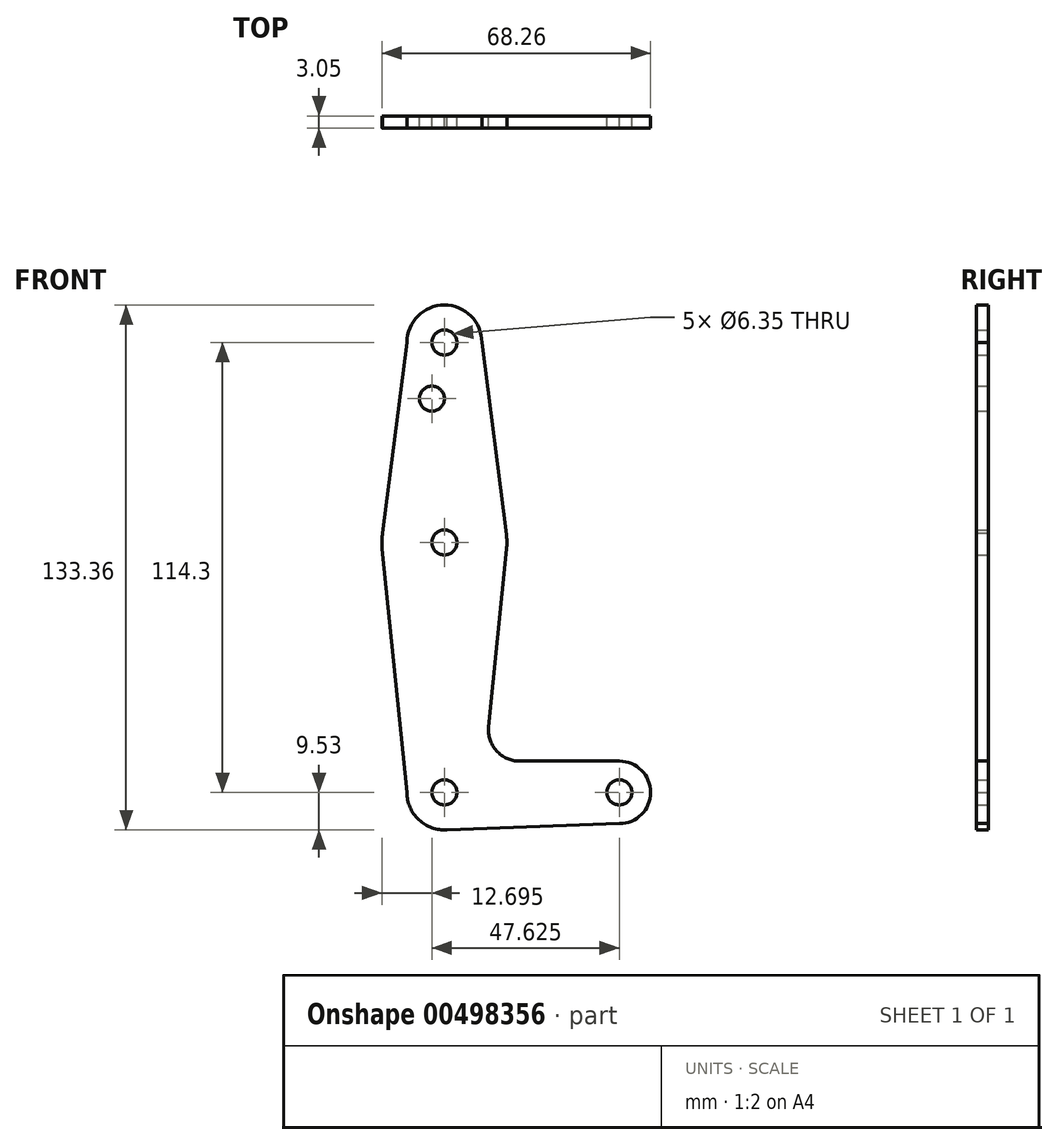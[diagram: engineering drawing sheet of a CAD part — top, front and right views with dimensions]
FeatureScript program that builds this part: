
annotation { "Feature Type Name" : "Feature", "Feature Type Description" : "" }
export const myFeature = defineFeature(function(context is Context, id is Id, definition is map)
    precondition{}
    {
        {
            var Q0;
            Q0=qCreatedBy(makeId("Front.planeOp"),FACE);
            var sketch = newSketch(context, id + "F0", { "sketchPlane" : qUnion([Q0])});
            skLineSegment(sketch, "E0", {"start": v(0, 0) * mm, "end": v(0, 114.3) * mm, "construction": true});
            skLineSegment(sketch, "E1", {"start": v(0, 0) * mm, "end": v(44.45, 0) * mm, "construction": true});
            skCircle(sketch, "E2", {"center": v(0, 114.3) * mm, "radius": 9.53 * mm});
            skCircle(sketch, "E3", {"center": v(0, 63.5) * mm, "radius": 15.88 * mm});
            skCircle(sketch, "E4", {"center": v(0, 0) * mm, "radius": 9.53 * mm});
            skCircle(sketch, "E5", {"center": v(44.45, 0) * mm, "radius": 7.94 * mm});
            skLineSegment(sketch, "E6", {"start": v(-9.53, 0) * mm, "end": v(-15.8, 61.9) * mm});
            skLineSegment(sketch, "E7", {"start": v(-9.53, 114.3) * mm, "end": v(-15.8, 65.1) * mm});
            skLineSegment(sketch, "E8", {"start": v(9.52, 114.3) * mm, "end": v(15.75, 65.5) * mm});
            skLineSegment(sketch, "E9", {"start": v(0, -9.52) * mm, "end": v(44.45, -7.94) * mm});
            skCircle(sketch, "E10", {"center": v(0, 114.3) * mm, "radius": 3.18 * mm});
            skCircle(sketch, "E11", {"center": v(-3.18, 100.03) * mm, "radius": 3.18 * mm});
            skCircle(sketch, "E12", {"center": v(0, 63.5) * mm, "radius": 3.18 * mm});
            skCircle(sketch, "E13", {"center": v(0, 0) * mm, "radius": 3.18 * mm});
            skCircle(sketch, "E14", {"center": v(44.45, 0) * mm, "radius": 3.18 * mm});
            skLineSegment(sketch, "E15", {"start": v(15.8, 61.9) * mm, "end": v(11.22, 16.69) * mm});
            skLineSegment(sketch, "E16", {"start": v(44.45, 7.94) * mm, "end": v(19.12, 7.94) * mm});
            skArc(sketch, "E17.filletArc", {"start": v(11.22, 16.69) * mm, "mid": v(13.23, 10.56) * mm, "end": v(19.12, 7.94) * mm});
            skSolve(sketch);
        }
        {
            var Q0;
            Q0 = qSketchRegion(id + "F0", true);
            extrude(context, id + "F1", {"entities" : qUnion([Q0]), "depth" : 3.05 * mm});
        }
    });
